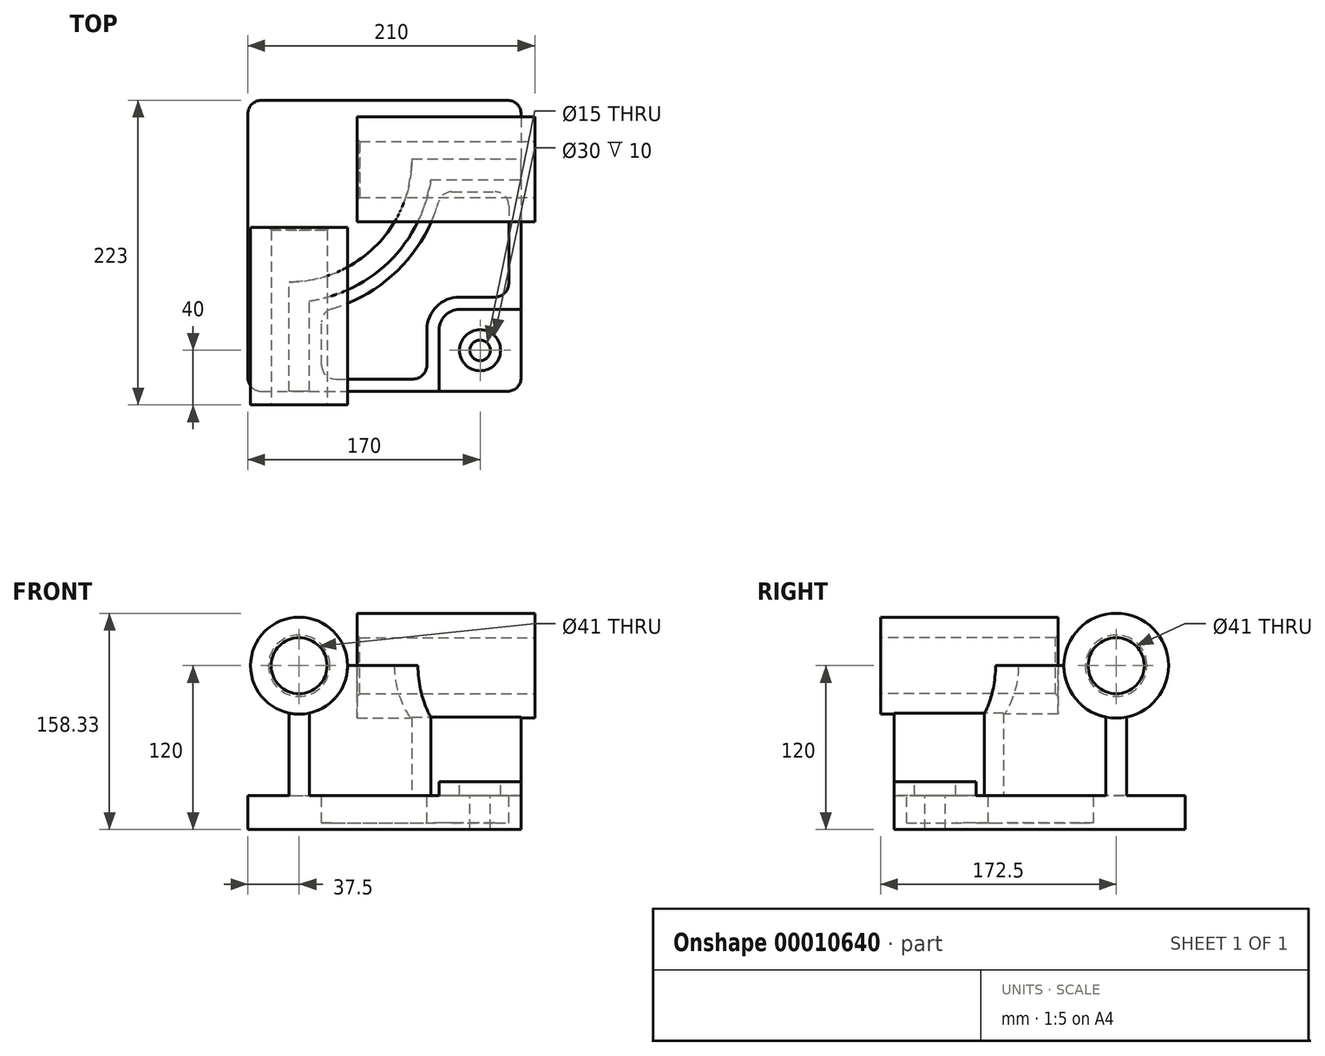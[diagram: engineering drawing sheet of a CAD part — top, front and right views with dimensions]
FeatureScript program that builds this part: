
annotation { "Feature Type Name" : "Feature", "Feature Type Description" : "" }
export const myFeature = defineFeature(function(context is Context, id is Id, definition is map)
    precondition{}
    {
        {
            assignVariable(context, id + "F0", {"name" : "D", "anyValue" : 130});
        }
        {
            var Q0;
            Q0=qCreatedBy(makeId("Top.planeOp"),FACE);
            var sketch = newSketch(context, id + "F1", { "sketchPlane" : qUnion([Q0])});
            skLineSegment(sketch, "E0.rect.bottom", {"start": v(-100, 106.5) * mm, "end": v(100, 106.5) * mm});
            skLineSegment(sketch, "E0.rect.top", {"start": v(-100, -106.5) * mm, "end": v(100, -106.5) * mm});
            skLineSegment(sketch, "E0.rect.left", {"start": v(-100, 106.5) * mm, "end": v(-100, -106.5) * mm});
            skLineSegment(sketch, "E0.rect.right", {"start": v(100, 106.5) * mm, "end": v(100, -106.5) * mm});
            skPoint(sketch, "E0.rect.middle", {"position": v(0, 0) * mm});
            skSolve(sketch);
        }
        {
            var Q0;
            Q0 = qSketchRegion(id + "F1", true);
            extrude(context, id + "F2", {"entities" : qUnion([Q0]), "depth" : 25 * mm});
        }
        {
            var Q0;
            Q0=makeQuery(id+"F2.opExtrude","CAP_FACE",FACE,{"disambiguationData":[OSD([sQuery(id+"F1.wireOp",EDGE,"E0.rect.bottom"),sQuery(id+"F1.wireOp",EDGE,"E0.rect.top"),sQuery(id+"F1.wireOp",EDGE,"E0.rect.left"),sQuery(id+"F1.wireOp",EDGE,"E0.rect.right")])],"isStart":false});
            var sketch = newSketch(context, id + "F3", { "sketchPlane" : qUnion([Q0])});
            skLineSegment(sketch, "E1.bottom", {"start": v(100, -106.5) * mm, "end": v(40, -106.5) * mm});
            skLineSegment(sketch, "E1.top", {"start": v(100, -46.5) * mm, "end": v(40, -46.5) * mm});
            skLineSegment(sketch, "E1.left", {"start": v(100, -106.5) * mm, "end": v(100, -46.5) * mm});
            skLineSegment(sketch, "E1.right", {"start": v(40, -106.5) * mm, "end": v(40, -46.5) * mm});
            skSolve(sketch);
        }
        {
            var Q0;
            Q0 = qSketchRegion(id + "F3", true);
            extrude(context, id + "F4", {"entities" : qUnion([Q0]), "operationType" : NewBodyOperationType.ADD, "depth" : 10 * mm});
        }
        {
            var Q0;
            Q0=makeQuery(id+"F4.opExtrude","CAP_FACE",FACE,{"disambiguationData":[OSD([sQuery(id+"F3.wireOp",EDGE,"E1.bottom"),sQuery(id+"F3.wireOp",EDGE,"E1.top"),sQuery(id+"F3.wireOp",EDGE,"E1.left"),sQuery(id+"F3.wireOp",EDGE,"E1.right")])],"isStart":false});
            var sketch = newSketch(context, id + "F5", { "sketchPlane" : qUnion([Q0])});
            skCircle(sketch, "E2", {"center": v(70, -76.5) * mm, "radius": 7.5 * mm});
            skSolve(sketch);
        }
        {
            var Q0;
            Q0 = qSketchRegion(id + "F5", true);
            extrude(context, id + "F6", {"entities" : qUnion([Q0]), "operationType" : NewBodyOperationType.REMOVE, "endBound" : BoundingType.THROUGH_ALL, "oppositeDirection" : true, "depth" : 25 * mm});
        }
        {
            var Q0;
            Q0=makeQuery(id+"F4.opExtrude","CAP_FACE",FACE,{"disambiguationData":[OSD([sQuery(id+"F3.wireOp",EDGE,"E1.bottom"),sQuery(id+"F3.wireOp",EDGE,"E1.top"),sQuery(id+"F3.wireOp",EDGE,"E1.left"),sQuery(id+"F3.wireOp",EDGE,"E1.right")])],"isStart":false});
            var sketch = newSketch(context, id + "F7", { "sketchPlane" : qUnion([Q0])});
            skCircle(sketch, "E3", {"center": v(70, -76.5) * mm, "radius": 15 * mm});
            skSolve(sketch);
        }
        {
            var Q0;
            Q0 = qSketchRegion(id + "F7", true);
            extrude(context, id + "F8", {"entities" : qUnion([Q0]), "operationType" : NewBodyOperationType.REMOVE, "oppositeDirection" : true, "depth" : 10 * mm});
        }
        {
            var Q0;
            Q0=makeQuery(id+"F2.opExtrude","CAP_FACE",FACE,{"disambiguationData":[OSD([sQuery(id+"F1.wireOp",EDGE,"E0.rect.bottom"),sQuery(id+"F1.wireOp",EDGE,"E0.rect.top"),sQuery(id+"F1.wireOp",EDGE,"E0.rect.left"),sQuery(id+"F1.wireOp",EDGE,"E0.rect.right")])],"isStart":false});
            var sketch = newSketch(context, id + "F9", { "sketchPlane" : qUnion([Q0])});
            skLineSegment(sketch, "E4", {"start": v(-70, -106.5) * mm, "end": v(-70, -26.5) * mm});
            skArc(sketch, "E5", {"start": v(-70, -26.5) * mm, "mid": v(-6.36, -0.14) * mm, "end": v(20, 63.5) * mm});
            skLineSegment(sketch, "E6", {"start": v(20, 63.5) * mm, "end": v(100, 63.5) * mm});
            skLineSegment(sketch, "E7.0", {"start": v(33.92, 48.5) * mm, "end": v(100, 48.5) * mm});
            skArc(sketch, "E7.1", {"start": v(-55, -40.42) * mm, "mid": v(4.25, -10.75) * mm, "end": v(33.92, 48.5) * mm});
            skLineSegment(sketch, "E7.2", {"start": v(-55, -106.5) * mm, "end": v(-55, -40.42) * mm});
            skLineSegment(sketch, "E8", {"start": v(-70, -106.5) * mm, "end": v(-55, -106.5) * mm});
            skLineSegment(sketch, "E9", {"start": v(100, 63.5) * mm, "end": v(100, 48.5) * mm});
            skSolve(sketch);
        }
        {
            var Q0;
            Q0 = qSketchRegion(id + "F9", true);
            extrude(context, id + "F10", {"entities" : qUnion([Q0]), "operationType" : NewBodyOperationType.ADD, "depth" : 95 * mm});
        }
        {
            var Q0;
            Q0=makeQuery(id+"F10.boolean.opBoolean","MERGE",FACE,{"derivedFrom":[makeQuery(id+"F4.boolean.opBoolean","MERGE",FACE,{"derivedFrom":[makeQuery(id+"F2.opExtrude","SWEPT_FACE",FACE,{"disambiguationData":[OSD([sQuery(id+"F1.wireOp",EDGE,"E0.rect.top")])]}),makeQuery(id+"F4.opExtrude","SWEPT_FACE",FACE,{"disambiguationData":[OSD([sQuery(id+"F3.wireOp",EDGE,"E1.bottom")])]})]}),makeQuery(id+"F10.opExtrude","SWEPT_FACE",FACE,{"disambiguationData":[OSD([sQuery(id+"F9.wireOp",EDGE,"E8")])]})]});
            cPlane(context, id + "F11", {"entities" : qUnion([Q0]), "cplaneType" : CPlaneType.OFFSET, "offset" : 10 * mm, "width" : 150 * mm, "height" : 150 * mm});
        }
        {
            var Q0;
            Q0=qCreatedBy(id+"F11.planeOp",FACE);
            var sketch = newSketch(context, id + "F12", { "sketchPlane" : qUnion([Q0])});
            skLineSegment(sketch, "E10.0", {"start": v(-70, 120) * mm, "end": v(-55, 120) * mm, "construction": true});
            skCircle(sketch, "E11", {"center": v(-62.5, 120) * mm, "radius": 35.5 * mm});
            skSolve(sketch);
        }
        {
            var Q0;
            Q0 = qSketchRegion(id + "F12", true);
            extrude(context, id + "F13", {"entities" : qUnion([Q0]), "operationType" : NewBodyOperationType.ADD, "oppositeDirection" : true, "depth" : (getVariable(context, 'D')) * mm});
        }
        {
            var Q0;
            Q0=makeQuery(id+"F10.boolean.opBoolean","MERGE",FACE,{"derivedFrom":[makeQuery(id+"F4.boolean.opBoolean","MERGE",FACE,{"derivedFrom":[makeQuery(id+"F2.opExtrude","SWEPT_FACE",FACE,{"disambiguationData":[OSD([sQuery(id+"F1.wireOp",EDGE,"E0.rect.right")])]}),makeQuery(id+"F4.opExtrude","SWEPT_FACE",FACE,{"disambiguationData":[OSD([sQuery(id+"F3.wireOp",EDGE,"E1.left")])]})]}),makeQuery(id+"F10.opExtrude","SWEPT_FACE",FACE,{"disambiguationData":[OSD([sQuery(id+"F9.wireOp",EDGE,"E9")])]})]});
            cPlane(context, id + "F14", {"entities" : qUnion([Q0]), "cplaneType" : CPlaneType.OFFSET, "offset" : 10 * mm, "width" : 150 * mm, "height" : 150 * mm});
        }
        {
            var Q0;
            Q0=qCreatedBy(id+"F14.planeOp",FACE);
            var sketch = newSketch(context, id + "F15", { "sketchPlane" : qUnion([Q0])});
            skLineSegment(sketch, "E12.0", {"start": v(63.5, 120) * mm, "end": v(48.5, 120) * mm, "construction": true});
            skCircle(sketch, "E13", {"center": v(56, 120) * mm, "radius": 38.33 * mm});
            skSolve(sketch);
        }
        {
            var Q0;
            Q0 = qSketchRegion(id + "F15", true);
            extrude(context, id + "F16", {"entities" : qUnion([Q0]), "operationType" : NewBodyOperationType.ADD, "oppositeDirection" : true, "depth" : (getVariable(context, 'D')) * mm});
        }
        {
            var Q0;
            Q0=makeQuery(id+"F13.opExtrude","CAP_FACE",FACE,{"disambiguationData":[OSD([sQuery(id+"F12.wireOp",EDGE,"E11")])],"isStart":true});
            var sketch = newSketch(context, id + "F17", { "sketchPlane" : qUnion([Q0])});
            skCircle(sketch, "E14", {"center": v(-62.5, 120) * mm, "radius": 20.5 * mm});
            skSolve(sketch);
        }
        {
            var Q0;
            Q0 = qSketchRegion(id + "F17", true);
            extrude(context, id + "F18", {"entities" : qUnion([Q0]), "operationType" : NewBodyOperationType.REMOVE, "endBound" : BoundingType.THROUGH_ALL, "oppositeDirection" : true, "depth" : 25 * mm});
        }
        {
            var Q0;
            Q0=makeQuery(id+"F16.opExtrude","CAP_FACE",FACE,{"disambiguationData":[OSD([sQuery(id+"F15.wireOp",EDGE,"E13")])],"isStart":true});
            var sketch = newSketch(context, id + "F19", { "sketchPlane" : qUnion([Q0])});
            skCircle(sketch, "E15", {"center": v(56, 120) * mm, "radius": 20.5 * mm});
            skSolve(sketch);
        }
        {
            var Q0;
            Q0 = qSketchRegion(id + "F19", true);
            extrude(context, id + "F20", {"entities" : qUnion([Q0]), "operationType" : NewBodyOperationType.REMOVE, "endBound" : BoundingType.THROUGH_ALL, "oppositeDirection" : true, "depth" : 25 * mm});
        }
        {
            var Q0;
            Q0=makeQuery(id+"F18.boolean.opBoolean","COPY",EDGE,{"derivedFrom":makeQuery(id+"F18.opExtrude","CAP_EDGE",EDGE,{"disambiguationData":[OSD([sQuery(id+"F17.wireOp",EDGE,"E14")])],"isStart":true})});
            var Q1;
            Q1=makeQuery(id+"F20.boolean.opBoolean","COPY",EDGE,{"derivedFrom":makeQuery(id+"F20.opExtrude","CAP_EDGE",EDGE,{"disambiguationData":[OSD([sQuery(id+"F19.wireOp",EDGE,"E15")])],"isStart":true})});
            var Q2;
            Q2=makeQuery(id+"F18.boolean.opBoolean","INTERSECT",EDGE,{"derivedFrom":[makeQuery(id+"F13.opExtrude","CAP_FACE",FACE,{"disambiguationData":[OSD([sQuery(id+"F12.wireOp",EDGE,"E11")])],"isStart":false}),makeQuery(id+"F18.opExtrude","SWEPT_FACE",FACE,{"disambiguationData":[OSD([sQuery(id+"F17.wireOp",EDGE,"E14")])]})]});
            var Q3;
            Q3=makeQuery(id+"F20.boolean.opBoolean","INTERSECT",EDGE,{"derivedFrom":[makeQuery(id+"F16.opExtrude","CAP_FACE",FACE,{"disambiguationData":[OSD([sQuery(id+"F15.wireOp",EDGE,"E13")])],"isStart":false}),makeQuery(id+"F20.opExtrude","SWEPT_FACE",FACE,{"disambiguationData":[OSD([sQuery(id+"F19.wireOp",EDGE,"E15")])]})]});
            chamfer(context, id + "F21", {"entities" : qUnion([Q0, Q1, Q2, Q3]), "chamferType" : ChamferType.OFFSET_ANGLE, "width" : 2 * mm, "oppositeDirection" : false, "angle" : 45 * degree, "tangentPropagation" : true});
        }
        {
            var Q0;
            Q0=makeQuery(id+"F4.opExtrude","SWEPT_EDGE",EDGE,{"disambiguationData":[OSD([sQuery(id+"F3.wireOp",EDGE,"E1.top"),sQuery(id+"F3.wireOp",EDGE,"E1.right")])]});
            fillet(context, id + "F22", {"entities" : qUnion([Q0]), "radius" : 15 * mm, "tangentPropagation" : true, "allowEdgeOverflow" : false});
        }
        {
            var Q0;
            {var subQ0=sQuery(id+"F1.wireOp",EDGE,"E0.rect.top");var subQ1=sQuery(id+"F1.wireOp",EDGE,"E0.rect.right");Q0=makeQuery(id+"F10.boolean.opBoolean","SPLIT",FACE,{"disambiguationData":[TD([makeQuery(id+"F4.opExtrude","SWEPT_FACE",FACE,{"disambiguationData":[OSD([sQuery(id+"F3.wireOp",EDGE,"E1.top")])]})])],"derivedFrom":makeQuery(id+"F2.opExtrude","CAP_FACE",FACE,{"disambiguationData":[OSD([sQuery(id+"F1.wireOp",EDGE,"E0.rect.bottom"),subQ0,sQuery(id+"F1.wireOp",EDGE,"E0.rect.left"),subQ1])],"isStart":false})});}
            var sketch = newSketch(context, id + "F23", { "sketchPlane" : qUnion([Q0])});
            skLineSegment(sketch, "E16.0", {"start": v(-46, -97.5) * mm, "end": v(31, -97.5) * mm});
            skLineSegment(sketch, "E16.1", {"start": v(31, -97.5) * mm, "end": v(31, -61.5) * mm});
            skLineSegment(sketch, "E16.2", {"start": v(-46, -97.5) * mm, "end": v(-46, -47.95) * mm});
            skArc(sketch, "E16.3", {"start": v(31, -61.5) * mm, "mid": v(38.03, -44.53) * mm, "end": v(55, -37.5) * mm});
            skArc(sketch, "E16.4", {"start": v(-46, -47.95) * mm, "mid": v(10.61, -17.11) * mm, "end": v(41.45, 39.5) * mm});
            skLineSegment(sketch, "E16.5", {"start": v(41.45, 39.5) * mm, "end": v(91, 39.5) * mm});
            skLineSegment(sketch, "E16.6", {"start": v(91, 39.5) * mm, "end": v(91, -37.5) * mm});
            skLineSegment(sketch, "E16.7", {"start": v(91, -37.5) * mm, "end": v(55, -37.5) * mm});
            skSolve(sketch);
        }
        {
            var Q0;
            Q0 = qSketchRegion(id + "F23", true);
            extrude(context, id + "F24", {"entities" : qUnion([Q0]), "operationType" : NewBodyOperationType.REMOVE, "oppositeDirection" : true, "depth" : 20 * mm});
        }
        {
            var Q0;
            Q0=makeQuery(id+"F24.boolean.opBoolean","COPY",EDGE,{"derivedFrom":makeQuery(id+"F24.opExtrude","SWEPT_EDGE",EDGE,{"disambiguationData":[OSD([sQuery(id+"F23.wireOp",EDGE,"E16.2"),sQuery(id+"F23.wireOp",EDGE,"E16.4")])]})});
            var Q1;
            Q1=makeQuery(id+"F24.boolean.opBoolean","COPY",EDGE,{"derivedFrom":makeQuery(id+"F24.opExtrude","SWEPT_EDGE",EDGE,{"disambiguationData":[OSD([sQuery(id+"F23.wireOp",EDGE,"E16.4"),sQuery(id+"F23.wireOp",EDGE,"E16.5")])]})});
            var Q2;
            Q2=makeQuery(id+"F24.boolean.opBoolean","COPY",EDGE,{"derivedFrom":makeQuery(id+"F24.opExtrude","SWEPT_EDGE",EDGE,{"disambiguationData":[OSD([sQuery(id+"F23.wireOp",EDGE,"E16.5"),sQuery(id+"F23.wireOp",EDGE,"E16.6")])]})});
            var Q3;
            Q3=makeQuery(id+"F24.boolean.opBoolean","COPY",EDGE,{"derivedFrom":makeQuery(id+"F24.opExtrude","SWEPT_EDGE",EDGE,{"disambiguationData":[OSD([sQuery(id+"F23.wireOp",EDGE,"E16.6"),sQuery(id+"F23.wireOp",EDGE,"E16.7")])]})});
            var Q4;
            Q4=makeQuery(id+"F24.boolean.opBoolean","COPY",EDGE,{"derivedFrom":makeQuery(id+"F24.opExtrude","SWEPT_EDGE",EDGE,{"disambiguationData":[OSD([sQuery(id+"F23.wireOp",EDGE,"E16.0"),sQuery(id+"F23.wireOp",EDGE,"E16.2")])]})});
            var Q5;
            Q5=makeQuery(id+"F24.boolean.opBoolean","COPY",EDGE,{"derivedFrom":makeQuery(id+"F24.opExtrude","SWEPT_EDGE",EDGE,{"disambiguationData":[OSD([sQuery(id+"F23.wireOp",EDGE,"E16.0"),sQuery(id+"F23.wireOp",EDGE,"E16.1")])]})});
            fillet(context, id + "F25", {"entities" : qUnion([Q0, Q1, Q2, Q3, Q4, Q5]), "radius" : 10 * mm, "tangentPropagation" : true, "allowEdgeOverflow" : false});
        }
        {
            var Q0;
            Q0=makeQuery(id+"F4.boolean.opBoolean","MERGE",EDGE,{"derivedFrom":[makeQuery(id+"F2.opExtrude","SWEPT_EDGE",EDGE,{"disambiguationData":[OSD([sQuery(id+"F1.wireOp",EDGE,"E0.rect.top"),sQuery(id+"F1.wireOp",EDGE,"E0.rect.right")])]}),makeQuery(id+"F4.opExtrude","SWEPT_EDGE",EDGE,{"disambiguationData":[OSD([sQuery(id+"F3.wireOp",EDGE,"E1.bottom"),sQuery(id+"F3.wireOp",EDGE,"E1.left")])]})]});
            var Q1;
            Q1=makeQuery(id+"F2.opExtrude","SWEPT_EDGE",EDGE,{"disambiguationData":[OSD([sQuery(id+"F1.wireOp",EDGE,"E0.rect.bottom"),sQuery(id+"F1.wireOp",EDGE,"E0.rect.right")])]});
            var Q2;
            Q2=makeQuery(id+"F2.opExtrude","SWEPT_EDGE",EDGE,{"disambiguationData":[OSD([sQuery(id+"F1.wireOp",EDGE,"E0.rect.bottom"),sQuery(id+"F1.wireOp",EDGE,"E0.rect.left")])]});
            var Q3;
            Q3=makeQuery(id+"F2.opExtrude","SWEPT_EDGE",EDGE,{"disambiguationData":[OSD([sQuery(id+"F1.wireOp",EDGE,"E0.rect.top"),sQuery(id+"F1.wireOp",EDGE,"E0.rect.left")])]});
            fillet(context, id + "F26", {"entities" : qUnion([Q0, Q1, Q2, Q3]), "radius" : 10 * mm, "tangentPropagation" : true, "allowEdgeOverflow" : false});
        }
    });
